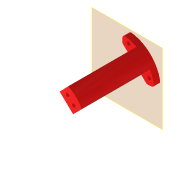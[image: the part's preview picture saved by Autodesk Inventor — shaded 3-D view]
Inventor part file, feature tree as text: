
AUTODESK INVENTOR PART (.ipt)
format: ipt  version: 2022 (Build 260153000, 153)  size: 157,184 bytes
history: native  units: mm
features: extrude x3, sketch x3, projected_geometry x2, other x2, plane x1, fillet x1, reference x1
ambient origin geometry x8: Origin, YZ Plane, XZ Plane, XY Plane, X Axis, Y Axis, Z Axis, Center Point
bodies: Volumenkörper1 (feature_tree)
feature tree (13):
  plane  "Arbeitsebene1"
  extrude  "Extrusion1"  Depth=5.0mm
  fillet  "Rundung1"  Radius=5.0mm
  extrude  "Extrusion2"  Depth=5.0mm TaperAngle=0.0deg
  extrude  "Extrusion3"  Depth=20.0mm
  sketch  "Skizze1"  dims[d0=1.0mm d1=6.0mm d2=5.0mm]
  reference  "Referenz1"
  sketch  "Skizze2"  dims[d3=5.0mm d4=5.0mm d5=0.0mm]
  projected_geometry  "Projizierte Kontur1"
  sketch  "Skizze3"  dims[d6=3.0mm d7=3.0mm d8=2.0mm d9=4.0mm d10=4.0mm d11=55.0mm d12=0.0mm d13=2.8mm d14=2.8mm d15=4.0mm d16=4.0mm d17=5.0mm d18=5.0mm d19=20.0mm d20=0.0mm]
  projected_geometry  "Projizierte Kontur2"
  other  "Assembly_Matchboxscope_injectionmolded_holo.iam"
  other  "IM_Matchboxscope_base:1"
